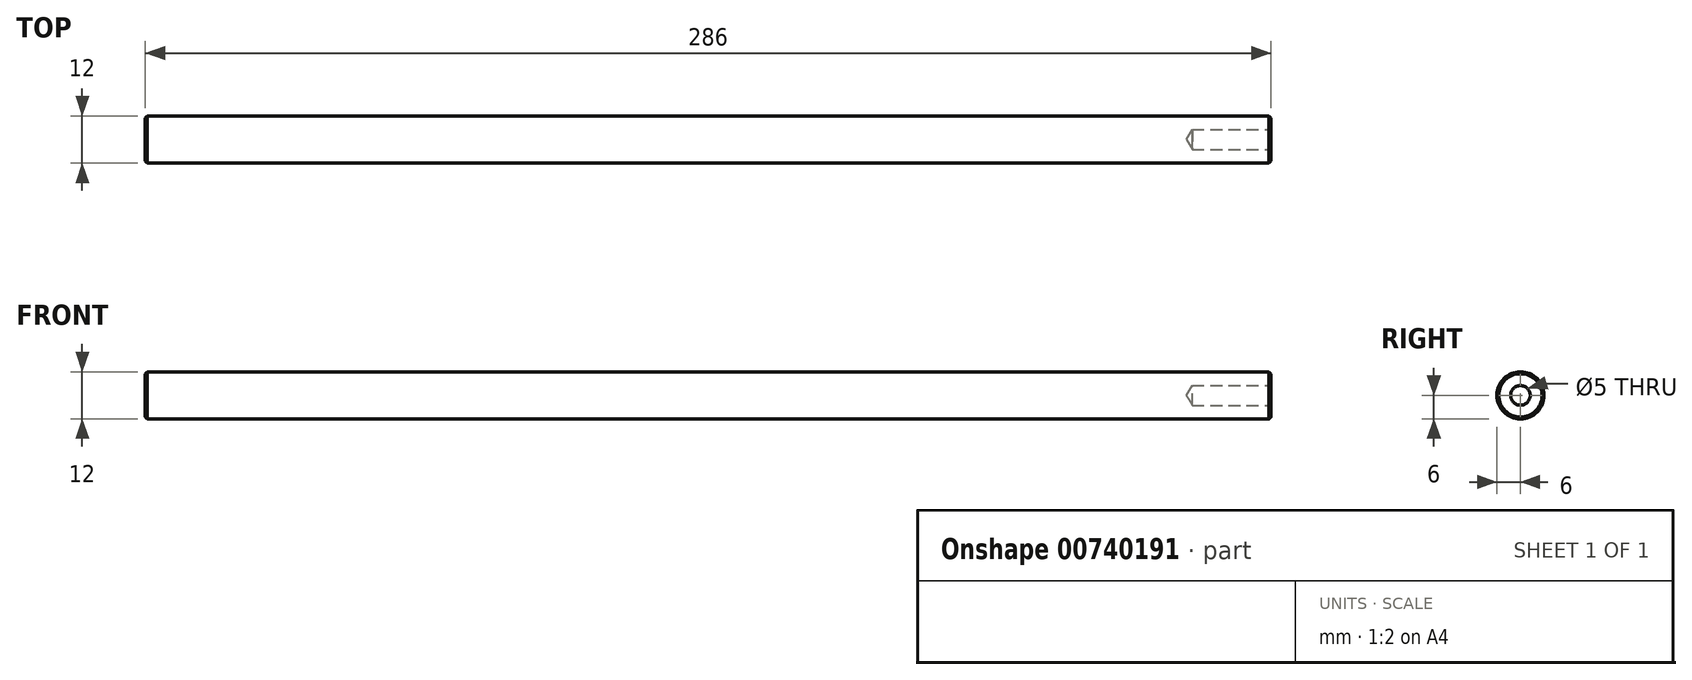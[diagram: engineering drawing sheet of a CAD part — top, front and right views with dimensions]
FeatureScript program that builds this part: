
annotation { "Feature Type Name" : "Feature", "Feature Type Description" : "" }
export const myFeature = defineFeature(function(context is Context, id is Id, definition is map)
    precondition{}
    {
        {
            var Q0;
            Q0=qCreatedBy(makeId("Right.planeOp"),FACE);
            var sketch = newSketch(context, id + "F0", { "sketchPlane" : qUnion([Q0])});
            skCircle(sketch, "E0", {"center": v(0, 0) * mm, "radius": 6 * mm});
            skSolve(sketch);
        }
        {
            var Q0;
            Q0=makeQuery(id+"F0.imprint","IMPRINT",FACE,{"disambiguationData":[TD([[makeQuery(id+"F0.imprint","IMPRINT",EDGE,{"derivedFrom":sQuery(id+"F0.wireOp",EDGE,"E0")}),1.0]])]});
            extrude(context, id + "F1", {"entities" : qUnion([Q0]), "depth" : 286 * mm, "offsetDistance" : 25 * mm, "symmetric" : true});
        }
        {
            var Q0;
            Q0=makeQuery(id+"F1.opExtrude","CAP_FACE",FACE,{"disambiguationData":[OSD([sQuery(id+"F0.wireOp",EDGE,"E0")])],"isStart":false});
            var sketch = newSketch(context, id + "F2", { "sketchPlane" : qUnion([Q0])});
            skCircle(sketch, "E1.0", {"center": v(0, 0) * mm, "radius": 6 * mm});
            skSolve(sketch);
        }
        {
            var Q0;
            Q0=sQuery(id+"F2.wireOp",VERTEX,"E1.0.center");
            var Q1;
            Q1=makeQuery(id+"F1.opExtrude","SWEPT_BODY",BODY,{"disambiguationData":[OSD([sQuery(id+"F0.wireOp",EDGE,"E0")])]});
            hole(context, id + "F3", {"style" : HoleStyle.SIMPLE, "endStyle" : HoleEndStyle.BLIND, "standardTappedOrClearance" : lookupTablePath({ "standard" : "ISO", "engagement" : "75%", "pitch" : "1 mm", "size" : "M6", "type" : "Tapped" }), "standardBlindInLast" : lookupTablePath({ "standard" : "ISO", "engagement" : "75%", "pitch" : "1 mm", "size" : "M6", "type" : "Tapped" }), "holeDiameter" : 5 * mm, "majorDiameter" : 6 * mm, "showTappedDepth" : true, "holeDepth" : 20 * mm, "isTappedThrough" : true, "tappedDepth" : 20 * mm, "tapClearance" : 0, "startFromSketch" : true, "locations" : qUnion([Q0]), "scope" : qUnion([Q1])});
        }
        {
            var Q0;
            Q0=makeQuery(id+"F1.opExtrude","CAP_EDGE",EDGE,{"disambiguationData":[OSD([sQuery(id+"F0.wireOp",EDGE,"E0")])],"isStart":false});
            var Q1;
            Q1=makeQuery(id+"F1.opExtrude","CAP_EDGE",EDGE,{"disambiguationData":[OSD([sQuery(id+"F0.wireOp",EDGE,"E0")])],"isStart":true});
            chamfer(context, id + "F4", {"entities" : qUnion([Q0, Q1]), "width" : 0.5 * mm, "tangentPropagation" : true});
        }
    });
